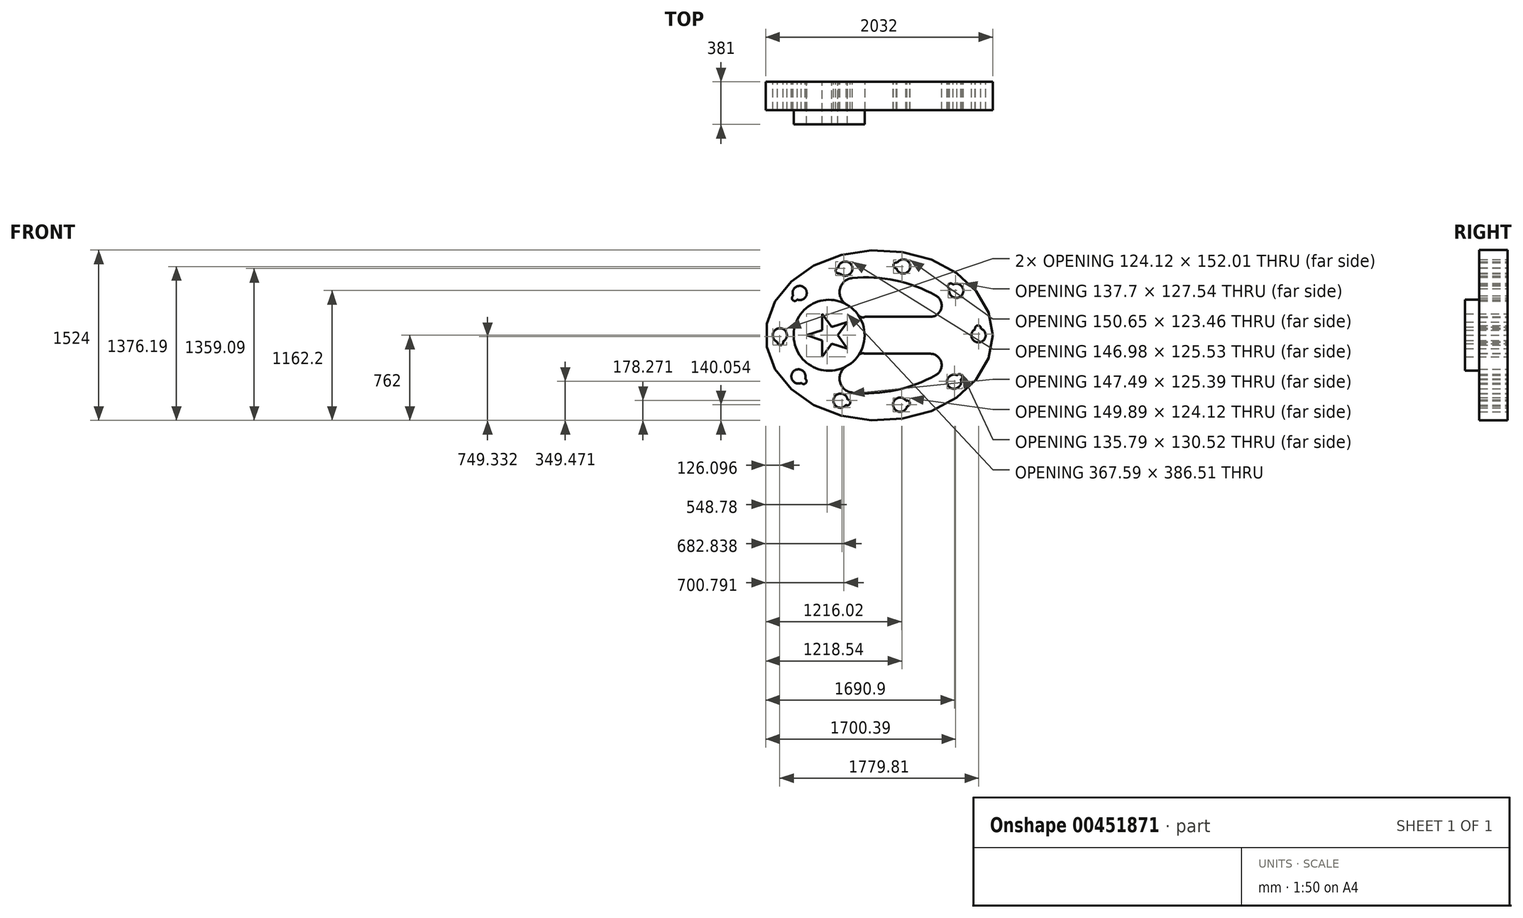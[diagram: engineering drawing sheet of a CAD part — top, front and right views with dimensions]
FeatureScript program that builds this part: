
annotation { "Feature Type Name" : "Feature", "Feature Type Description" : "" }
export const myFeature = defineFeature(function(context is Context, id is Id, definition is map)
    precondition{}
    {
        {
            var Q0;
            Q0=qCreatedBy(makeId("Front.planeOp"),FACE);
            var sketch = newSketch(context, id + "F0", { "sketchPlane" : qUnion([Q0])});
            skEllipse(sketch, "E0", {"center": v(0, 0) * mm, "majorRadius": 1016 * mm, "minorRadius": 762 * mm, "majorAxis": v(1, 0)});
            skCircle(sketch, "E1", {"center": v(-447.82, 0) * mm, "radius": 317.5 * mm});
            skArc(sketch, "E2", {"start": v(-187.82, 182.23) * mm, "mid": v(-159.63, 162.39) * mm, "end": v(-125.28, 165.1) * mm});
            skLineSegment(sketch, "E3", {"start": v(-125.28, 165.1) * mm, "end": v(457.62, 165.1) * mm});
            skArc(sketch, "E4", {"start": v(-240, 512.49) * mm, "mid": v(-351.77, 412.6) * mm, "end": v(-290.5, 275.78) * mm});
            skArc(sketch, "E5", {"start": v(457.62, 165.1) * mm, "mid": v(555.9, 240.93) * mm, "end": v(507.46, 355.23) * mm});
            skArc(sketch, "E6", {"start": v(507.46, 355.23) * mm, "mid": v(145.83, 491.38) * mm, "end": v(-240, 512.49) * mm});
            skLineSegment(sketch, "E7", {"start": v(-510.6, 193.25) * mm, "end": v(-423.83, 73.82) * mm});
            skLineSegment(sketch, "E8.1.0", {"start": v(-510.6, -193.25) * mm, "end": v(-423.83, -73.82) * mm});
            skLineSegment(sketch, "E8.1.1", {"start": v(-651.02, 0) * mm, "end": v(-510.6, 45.62) * mm});
            skLineSegment(sketch, "E8.2.0", {"start": v(-283.42, -119.44) * mm, "end": v(-370.2, 0) * mm});
            skLineSegment(sketch, "E8.2.1", {"start": v(-510.6, -193.25) * mm, "end": v(-510.6, -45.62) * mm});
            skLineSegment(sketch, "E8.3.1", {"start": v(-283.42, -119.44) * mm, "end": v(-423.83, -73.82) * mm});
            skLineSegment(sketch, "E8.4.0", {"start": v(-510.6, 193.25) * mm, "end": v(-510.6, 45.62) * mm});
            skLineSegment(sketch, "E8.4.1", {"start": v(-283.42, 119.44) * mm, "end": v(-370.2, 0) * mm});
            skFitSpline(sketch, "E9.0", {"points": [v(888.96, -7.37) * mm, v(889.02, 0) * mm, v(888.96, 7.37) * mm, v(888.72, 17.17) * mm, v(888.1, 29.4) * mm, v(886.9, 44.05) * mm, v(884.64, 63.52) * mm, v(880.63, 87.75) * mm, v(873.9, 116.67) * mm, v(865.26, 145.41) * mm, v(854.7, 173.95) * mm, v(842.22, 202.24) * mm, v(823, 239.6) * mm, v(799.9, 276.3) * mm, v(772.9, 312.12) * mm, v(750.71, 338.47) * mm, v(726.57, 364.24) * mm, v(704.83, 385.18) * mm, v(686.47, 401.56) * mm, v(672.23, 413.66) * mm, v(659.96, 423.58) * mm, v(649.9, 431.4) * mm, v(642.24, 437.23) * mm, v(634.47, 442.98) * mm, v(623.98, 450.56) * mm, v(610.63, 459.86) * mm, v(594.23, 470.72) * mm, v(571.88, 484.8) * mm, v(543.04, 501.65) * mm, v(507.09, 520.6) * mm, v(469.85, 538.25) * mm, v(418.6, 560) * mm, v(365.13, 578.95) * mm, v(309.76, 594.98) * mm, v(267.38, 605.5) * mm, v(224.23, 614.48) * mm, v(180.4, 621.9) * mm, v(135.98, 627.7) * mm, v(98.54, 631.2) * mm, v(68.38, 633.16) * mm, v(45.67, 634.22) * mm, v(26.67, 634.75) * mm, v(11.44, 634.96) * mm, v(0, 635.02) * mm, v(-11.44, 634.96) * mm, v(-26.67, 634.75) * mm, v(-45.67, 634.22) * mm, v(-68.38, 633.16) * mm, v(-98.54, 631.2) * mm, v(-135.98, 627.7) * mm, v(-180.4, 621.9) * mm, v(-224.23, 614.48) * mm, v(-267.38, 605.5) * mm, v(-309.76, 594.98) * mm, v(-365.13, 578.95) * mm, v(-418.6, 560) * mm, v(-469.85, 538.25) * mm, v(-507.09, 520.6) * mm, v(-543.04, 501.65) * mm, v(-571.88, 484.8) * mm, v(-594.23, 470.72) * mm, v(-610.63, 459.86) * mm, v(-623.98, 450.56) * mm, v(-634.47, 442.98) * mm, v(-642.24, 437.23) * mm, v(-649.9, 431.4) * mm, v(-659.96, 423.58) * mm, v(-672.23, 413.66) * mm, v(-686.47, 401.56) * mm, v(-704.83, 385.18) * mm, v(-726.57, 364.24) * mm, v(-750.71, 338.47) * mm, v(-772.9, 312.12) * mm, v(-799.9, 276.3) * mm, v(-823, 239.6) * mm, v(-842.22, 202.24) * mm, v(-854.7, 173.95) * mm, v(-865.26, 145.41) * mm, v(-873.9, 116.67) * mm, v(-880.63, 87.75) * mm, v(-884.64, 63.52) * mm, v(-886.9, 44.05) * mm, v(-888.1, 29.4) * mm, v(-888.72, 17.17) * mm, v(-888.96, 7.37) * mm, v(-889.02, 0) * mm, v(-888.96, -7.37) * mm, v(-888.72, -17.17) * mm, v(-888.1, -29.4) * mm, v(-886.9, -44.05) * mm, v(-884.64, -63.52) * mm, v(-880.63, -87.75) * mm, v(-873.9, -116.67) * mm, v(-865.26, -145.41) * mm, v(-854.7, -173.95) * mm, v(-842.22, -202.24) * mm, v(-823, -239.6) * mm, v(-799.9, -276.3) * mm, v(-772.9, -312.12) * mm, v(-750.71, -338.47) * mm, v(-726.57, -364.24) * mm, v(-704.83, -385.18) * mm, v(-686.47, -401.56) * mm, v(-672.23, -413.66) * mm, v(-659.96, -423.58) * mm, v(-649.9, -431.4) * mm, v(-642.24, -437.23) * mm, v(-634.47, -442.98) * mm, v(-623.98, -450.56) * mm, v(-610.63, -459.86) * mm, v(-594.23, -470.72) * mm, v(-571.88, -484.8) * mm, v(-543.04, -501.65) * mm, v(-507.09, -520.6) * mm, v(-469.85, -538.25) * mm, v(-418.6, -560) * mm, v(-365.13, -578.95) * mm, v(-309.76, -594.98) * mm, v(-267.38, -605.5) * mm, v(-224.23, -614.48) * mm, v(-180.4, -621.9) * mm, v(-135.98, -627.7) * mm, v(-98.54, -631.2) * mm, v(-68.38, -633.16) * mm, v(-45.67, -634.22) * mm, v(-26.67, -634.75) * mm, v(-11.44, -634.96) * mm, v(0, -635.02) * mm, v(11.44, -634.96) * mm, v(26.67, -634.75) * mm, v(45.67, -634.22) * mm, v(68.38, -633.16) * mm, v(98.54, -631.2) * mm, v(135.98, -627.7) * mm, v(180.4, -621.9) * mm, v(224.23, -614.48) * mm, v(267.38, -605.5) * mm, v(309.76, -594.98) * mm, v(365.13, -578.95) * mm, v(418.6, -560) * mm, v(469.85, -538.25) * mm, v(507.09, -520.6) * mm, v(543.04, -501.65) * mm, v(571.88, -484.8) * mm, v(594.23, -470.72) * mm, v(610.63, -459.86) * mm, v(623.98, -450.56) * mm, v(634.47, -442.98) * mm, v(642.24, -437.23) * mm, v(649.9, -431.4) * mm, v(659.96, -423.58) * mm, v(672.23, -413.66) * mm, v(686.47, -401.56) * mm, v(704.83, -385.18) * mm, v(726.57, -364.24) * mm, v(750.71, -338.47) * mm, v(772.9, -312.12) * mm, v(799.9, -276.3) * mm, v(823, -239.6) * mm, v(842.22, -202.24) * mm, v(854.7, -173.95) * mm, v(865.26, -145.41) * mm, v(873.9, -116.67) * mm, v(880.63, -87.75) * mm, v(884.64, -63.52) * mm, v(886.9, -44.05) * mm, v(888.1, -29.4) * mm, v(888.72, -17.17) * mm, v(888.96, -7.37) * mm, v(889.02, 0) * mm, v(888.96, 7.37) * mm], "construction": true});
            skArc(sketch, "E10", {"start": v(860.02, 56.5) * mm, "mid": v(893.52, -63.34) * mm, "end": v(909.66, 60.04) * mm});
            skArc(sketch, "E11", {"start": v(909.66, 60.04) * mm, "mid": v(882.67, 88.67) * mm, "end": v(860.02, 56.5) * mm});
            skArc(sketch, "E12", {"start": v(628.7, 416.03) * mm, "mid": v(739.09, 358.62) * mm, "end": v(660.02, 454.7) * mm});
            skLineSegment(sketch, "E13", {"start": v(619.82, 453.43) * mm, "end": v(619.82, 453.43) * mm});
            skLineSegment(sketch, "E14.trimOffspring", {"start": v(640.41, 438.57) * mm, "end": v(640.41, 438.57) * mm});
            skArc(sketch, "E15.trimOffspring", {"start": v(660.02, 454.7) * mm, "mid": v(620.68, 454.56) * mm, "end": v(628.7, 416.03) * mm});
            skArc(sketch, "E16", {"start": v(153.58, 600.11) * mm, "mid": v(277.86, 606.28) * mm, "end": v(161.1, 649.31) * mm});
            skLineSegment(sketch, "E17", {"start": v(177.49, 622.04) * mm, "end": v(177.49, 622.04) * mm});
            skArc(sketch, "E18.trimOffspring", {"start": v(161.1, 649.31) * mm, "mid": v(127.21, 629.32) * mm, "end": v(153.58, 600.11) * mm});
            skArc(sketch, "E19", {"start": v(-351.76, 556.3) * mm, "mid": v(-241.72, 614.39) * mm, "end": v(-365.72, 604.06) * mm});
            skArc(sketch, "E20", {"start": v(-365.72, 604.06) * mm, "mid": v(-388, 571.62) * mm, "end": v(-351.76, 556.3) * mm});
            skArc(sketch, "E21", {"start": v(-733.87, 319.18) * mm, "mid": v(-667.67, 424.54) * mm, "end": v(-769.87, 353.55) * mm});
            skArc(sketch, "E22", {"start": v(-769.87, 353.55) * mm, "mid": v(-772.92, 314.32) * mm, "end": v(-733.87, 319.18) * mm});
            skLineSegment(sketch, "E23", {"start": v(-887.37, -38.1) * mm, "end": v(-887.37, -38.1) * mm});
            skArc(sketch, "E24", {"start": v(-860.02, -56.5) * mm, "mid": v(-893.52, 63.34) * mm, "end": v(-909.66, -60.04) * mm});
            skArc(sketch, "E25.trimOffspring", {"start": v(-909.66, -60.04) * mm, "mid": v(-882.67, -88.67) * mm, "end": v(-860.02, -56.5) * mm});
            skArc(sketch, "E26", {"start": v(-662.6, -388.93) * mm, "mid": v(-769.38, -325.05) * mm, "end": v(-696.17, -425.67) * mm});
            skArc(sketch, "E27", {"start": v(-696.17, -425.67) * mm, "mid": v(-656.88, -427.86) * mm, "end": v(-662.6, -388.93) * mm});
            skLineSegment(sketch, "E28", {"start": v(-284.43, -601.19) * mm, "end": v(-284.43, -601.19) * mm});
            skArc(sketch, "E29", {"start": v(-295.9, -623.84) * mm, "mid": v(-259.93, -607.9) * mm, "end": v(-282.75, -575.84) * mm});
            skArc(sketch, "E30.trimOffspring", {"start": v(-282.75, -575.84) * mm, "mid": v(-406.9, -567.6) * mm, "end": v(-295.9, -623.84) * mm});
            skArc(sketch, "E31", {"start": v(240.48, -585.48) * mm, "mid": v(125.07, -632) * mm, "end": v(249.48, -634.43) * mm});
            skLineSegment(sketch, "E32", {"start": v(225.08, -614.03) * mm, "end": v(225.08, -614.03) * mm});
            skArc(sketch, "E33.trimOffspring", {"start": v(249.48, -634.43) * mm, "mid": v(274.96, -604.45) * mm, "end": v(240.48, -585.48) * mm});
            skLineSegment(sketch, "E34.trimOffspring", {"start": v(249.98, -609.04) * mm, "end": v(249.98, -609.04) * mm});
            skArc(sketch, "E35", {"start": v(697.3, -357.51) * mm, "mid": v(623.16, -457.45) * mm, "end": v(730.53, -394.56) * mm});
            skArc(sketch, "E36", {"start": v(730.53, -394.56) * mm, "mid": v(736.6, -355.68) * mm, "end": v(697.3, -357.51) * mm});
            skFitSpline(sketch, "E37.trimOffspring", {"points": [v(888.96, -7.37) * mm, v(889.02, 0) * mm, v(888.96, 7.37) * mm, v(888.72, 17.17) * mm, v(888.1, 29.4) * mm, v(886.9, 44.05) * mm, v(884.64, 63.52) * mm, v(880.63, 87.75) * mm, v(873.9, 116.67) * mm, v(865.26, 145.41) * mm, v(854.7, 173.95) * mm, v(842.22, 202.24) * mm, v(823, 239.6) * mm, v(799.9, 276.3) * mm, v(772.9, 312.12) * mm, v(750.71, 338.47) * mm, v(726.57, 364.24) * mm, v(704.83, 385.18) * mm, v(686.47, 401.56) * mm, v(672.23, 413.66) * mm, v(659.96, 423.58) * mm, v(649.9, 431.4) * mm, v(642.24, 437.23) * mm, v(634.47, 442.98) * mm, v(623.98, 450.56) * mm, v(610.63, 459.86) * mm, v(594.23, 470.72) * mm, v(571.88, 484.8) * mm, v(543.04, 501.65) * mm, v(507.09, 520.6) * mm, v(469.85, 538.25) * mm, v(418.6, 560) * mm, v(365.13, 578.95) * mm, v(309.76, 594.98) * mm, v(267.38, 605.5) * mm, v(224.23, 614.48) * mm, v(180.4, 621.9) * mm, v(135.98, 627.7) * mm, v(98.54, 631.2) * mm, v(68.38, 633.16) * mm, v(45.67, 634.22) * mm, v(26.67, 634.75) * mm, v(11.44, 634.96) * mm, v(0, 635.02) * mm, v(-11.44, 634.96) * mm, v(-26.67, 634.75) * mm, v(-45.67, 634.22) * mm, v(-68.38, 633.16) * mm, v(-98.54, 631.2) * mm, v(-135.98, 627.7) * mm, v(-180.4, 621.9) * mm, v(-224.23, 614.48) * mm, v(-267.38, 605.5) * mm, v(-309.76, 594.98) * mm, v(-365.13, 578.95) * mm, v(-418.6, 560) * mm, v(-469.85, 538.25) * mm, v(-507.09, 520.6) * mm, v(-543.04, 501.65) * mm, v(-571.88, 484.8) * mm, v(-594.23, 470.72) * mm, v(-610.63, 459.86) * mm, v(-623.98, 450.56) * mm, v(-634.47, 442.98) * mm, v(-642.24, 437.23) * mm, v(-649.9, 431.4) * mm, v(-659.96, 423.58) * mm, v(-672.23, 413.66) * mm, v(-686.47, 401.56) * mm, v(-704.83, 385.18) * mm, v(-726.57, 364.24) * mm, v(-750.71, 338.47) * mm, v(-772.9, 312.12) * mm, v(-799.9, 276.3) * mm, v(-823, 239.6) * mm, v(-842.22, 202.24) * mm, v(-854.7, 173.95) * mm, v(-865.26, 145.41) * mm, v(-873.9, 116.67) * mm, v(-880.63, 87.75) * mm, v(-884.64, 63.52) * mm, v(-886.9, 44.05) * mm, v(-888.1, 29.4) * mm, v(-888.72, 17.17) * mm, v(-888.96, 7.37) * mm, v(-889.02, 0) * mm, v(-888.96, -7.37) * mm, v(-888.72, -17.17) * mm, v(-888.1, -29.4) * mm, v(-886.9, -44.05) * mm, v(-884.64, -63.52) * mm, v(-880.63, -87.75) * mm, v(-873.9, -116.67) * mm, v(-865.26, -145.41) * mm, v(-854.7, -173.95) * mm, v(-842.22, -202.24) * mm, v(-823, -239.6) * mm, v(-799.9, -276.3) * mm, v(-772.9, -312.12) * mm, v(-750.71, -338.47) * mm, v(-726.57, -364.24) * mm, v(-704.83, -385.18) * mm, v(-686.47, -401.56) * mm, v(-672.23, -413.66) * mm, v(-659.96, -423.58) * mm, v(-649.9, -431.4) * mm, v(-642.24, -437.23) * mm, v(-634.47, -442.98) * mm, v(-623.98, -450.56) * mm, v(-610.63, -459.86) * mm, v(-594.23, -470.72) * mm, v(-571.88, -484.8) * mm, v(-543.04, -501.65) * mm, v(-507.09, -520.6) * mm, v(-469.85, -538.25) * mm, v(-418.6, -560) * mm, v(-365.13, -578.95) * mm, v(-309.76, -594.98) * mm, v(-267.38, -605.5) * mm, v(-224.23, -614.48) * mm, v(-180.4, -621.9) * mm, v(-135.98, -627.7) * mm, v(-98.54, -631.2) * mm, v(-68.38, -633.16) * mm, v(-45.67, -634.22) * mm, v(-26.67, -634.75) * mm, v(-11.44, -634.96) * mm, v(0, -635.02) * mm, v(11.44, -634.96) * mm, v(26.67, -634.75) * mm, v(45.67, -634.22) * mm, v(68.38, -633.16) * mm, v(98.54, -631.2) * mm, v(135.98, -627.7) * mm, v(180.4, -621.9) * mm, v(224.23, -614.48) * mm, v(267.38, -605.5) * mm, v(309.76, -594.98) * mm, v(365.13, -578.95) * mm, v(418.6, -560) * mm, v(469.85, -538.25) * mm, v(507.09, -520.6) * mm, v(543.04, -501.65) * mm, v(571.88, -484.8) * mm, v(594.23, -470.72) * mm, v(610.63, -459.86) * mm, v(623.98, -450.56) * mm, v(634.47, -442.98) * mm, v(642.24, -437.23) * mm, v(649.9, -431.4) * mm, v(659.96, -423.58) * mm, v(672.23, -413.66) * mm, v(686.47, -401.56) * mm, v(704.83, -385.18) * mm, v(726.57, -364.24) * mm, v(750.71, -338.47) * mm, v(772.9, -312.12) * mm, v(799.9, -276.3) * mm, v(823, -239.6) * mm, v(842.22, -202.24) * mm, v(854.7, -173.95) * mm, v(865.26, -145.41) * mm, v(873.9, -116.67) * mm, v(880.63, -87.75) * mm, v(884.64, -63.52) * mm, v(886.9, -44.05) * mm, v(888.1, -29.4) * mm, v(888.72, -17.17) * mm, v(888.96, -7.37) * mm, v(889.02, 0) * mm, v(888.96, 7.37) * mm], "construction": true});
            skFitSpline(sketch, "E38.trimOffspring", {"points": [v(888.96, -7.37) * mm, v(889.02, 0) * mm, v(888.96, 7.37) * mm, v(888.72, 17.17) * mm, v(888.1, 29.4) * mm, v(886.9, 44.05) * mm, v(884.64, 63.52) * mm, v(880.63, 87.75) * mm, v(873.9, 116.67) * mm, v(865.26, 145.41) * mm, v(854.7, 173.95) * mm, v(842.22, 202.24) * mm, v(823, 239.6) * mm, v(799.9, 276.3) * mm, v(772.9, 312.12) * mm, v(750.71, 338.47) * mm, v(726.57, 364.24) * mm, v(704.83, 385.18) * mm, v(686.47, 401.56) * mm, v(672.23, 413.66) * mm, v(659.96, 423.58) * mm, v(649.9, 431.4) * mm, v(642.24, 437.23) * mm, v(634.47, 442.98) * mm, v(623.98, 450.56) * mm, v(610.63, 459.86) * mm, v(594.23, 470.72) * mm, v(571.88, 484.8) * mm, v(543.04, 501.65) * mm, v(507.09, 520.6) * mm, v(469.85, 538.25) * mm, v(418.6, 560) * mm, v(365.13, 578.95) * mm, v(309.76, 594.98) * mm, v(267.38, 605.5) * mm, v(224.23, 614.48) * mm, v(180.4, 621.9) * mm, v(135.98, 627.7) * mm, v(98.54, 631.2) * mm, v(68.38, 633.16) * mm, v(45.67, 634.22) * mm, v(26.67, 634.75) * mm, v(11.44, 634.96) * mm, v(0, 635.02) * mm, v(-11.44, 634.96) * mm, v(-26.67, 634.75) * mm, v(-45.67, 634.22) * mm, v(-68.38, 633.16) * mm, v(-98.54, 631.2) * mm, v(-135.98, 627.7) * mm, v(-180.4, 621.9) * mm, v(-224.23, 614.48) * mm, v(-267.38, 605.5) * mm, v(-309.76, 594.98) * mm, v(-365.13, 578.95) * mm, v(-418.6, 560) * mm, v(-469.85, 538.25) * mm, v(-507.09, 520.6) * mm, v(-543.04, 501.65) * mm, v(-571.88, 484.8) * mm, v(-594.23, 470.72) * mm, v(-610.63, 459.86) * mm, v(-623.98, 450.56) * mm, v(-634.47, 442.98) * mm, v(-642.24, 437.23) * mm, v(-649.9, 431.4) * mm, v(-659.96, 423.58) * mm, v(-672.23, 413.66) * mm, v(-686.47, 401.56) * mm, v(-704.83, 385.18) * mm, v(-726.57, 364.24) * mm, v(-750.71, 338.47) * mm, v(-772.9, 312.12) * mm, v(-799.9, 276.3) * mm, v(-823, 239.6) * mm, v(-842.22, 202.24) * mm, v(-854.7, 173.95) * mm, v(-865.26, 145.41) * mm, v(-873.9, 116.67) * mm, v(-880.63, 87.75) * mm, v(-884.64, 63.52) * mm, v(-886.9, 44.05) * mm, v(-888.1, 29.4) * mm, v(-888.72, 17.17) * mm, v(-888.96, 7.37) * mm, v(-889.02, 0) * mm, v(-888.96, -7.37) * mm, v(-888.72, -17.17) * mm, v(-888.1, -29.4) * mm, v(-886.9, -44.05) * mm, v(-884.64, -63.52) * mm, v(-880.63, -87.75) * mm, v(-873.9, -116.67) * mm, v(-865.26, -145.41) * mm, v(-854.7, -173.95) * mm, v(-842.22, -202.24) * mm, v(-823, -239.6) * mm, v(-799.9, -276.3) * mm, v(-772.9, -312.12) * mm, v(-750.71, -338.47) * mm, v(-726.57, -364.24) * mm, v(-704.83, -385.18) * mm, v(-686.47, -401.56) * mm, v(-672.23, -413.66) * mm, v(-659.96, -423.58) * mm, v(-649.9, -431.4) * mm, v(-642.24, -437.23) * mm, v(-634.47, -442.98) * mm, v(-623.98, -450.56) * mm, v(-610.63, -459.86) * mm, v(-594.23, -470.72) * mm, v(-571.88, -484.8) * mm, v(-543.04, -501.65) * mm, v(-507.09, -520.6) * mm, v(-469.85, -538.25) * mm, v(-418.6, -560) * mm, v(-365.13, -578.95) * mm, v(-309.76, -594.98) * mm, v(-267.38, -605.5) * mm, v(-224.23, -614.48) * mm, v(-180.4, -621.9) * mm, v(-135.98, -627.7) * mm, v(-98.54, -631.2) * mm, v(-68.38, -633.16) * mm, v(-45.67, -634.22) * mm, v(-26.67, -634.75) * mm, v(-11.44, -634.96) * mm, v(0, -635.02) * mm, v(11.44, -634.96) * mm, v(26.67, -634.75) * mm, v(45.67, -634.22) * mm, v(68.38, -633.16) * mm, v(98.54, -631.2) * mm, v(135.98, -627.7) * mm, v(180.4, -621.9) * mm, v(224.23, -614.48) * mm, v(267.38, -605.5) * mm, v(309.76, -594.98) * mm, v(365.13, -578.95) * mm, v(418.6, -560) * mm, v(469.85, -538.25) * mm, v(507.09, -520.6) * mm, v(543.04, -501.65) * mm, v(571.88, -484.8) * mm, v(594.23, -470.72) * mm, v(610.63, -459.86) * mm, v(623.98, -450.56) * mm, v(634.47, -442.98) * mm, v(642.24, -437.23) * mm, v(649.9, -431.4) * mm, v(659.96, -423.58) * mm, v(672.23, -413.66) * mm, v(686.47, -401.56) * mm, v(704.83, -385.18) * mm, v(726.57, -364.24) * mm, v(750.71, -338.47) * mm, v(772.9, -312.12) * mm, v(799.9, -276.3) * mm, v(823, -239.6) * mm, v(842.22, -202.24) * mm, v(854.7, -173.95) * mm, v(865.26, -145.41) * mm, v(873.9, -116.67) * mm, v(880.63, -87.75) * mm, v(884.64, -63.52) * mm, v(886.9, -44.05) * mm, v(888.1, -29.4) * mm, v(888.72, -17.17) * mm, v(888.96, -7.37) * mm, v(889.02, 0) * mm, v(888.96, 7.37) * mm], "construction": true});
            skFitSpline(sketch, "E39.trimOffspring", {"points": [v(888.96, -7.37) * mm, v(889.02, 0) * mm, v(888.96, 7.37) * mm, v(888.72, 17.17) * mm, v(888.1, 29.4) * mm, v(886.9, 44.05) * mm, v(884.64, 63.52) * mm, v(880.63, 87.75) * mm, v(873.9, 116.67) * mm, v(865.26, 145.41) * mm, v(854.7, 173.95) * mm, v(842.22, 202.24) * mm, v(823, 239.6) * mm, v(799.9, 276.3) * mm, v(772.9, 312.12) * mm, v(750.71, 338.47) * mm, v(726.57, 364.24) * mm, v(704.83, 385.18) * mm, v(686.47, 401.56) * mm, v(672.23, 413.66) * mm, v(659.96, 423.58) * mm, v(649.9, 431.4) * mm, v(642.24, 437.23) * mm, v(634.47, 442.98) * mm, v(623.98, 450.56) * mm, v(610.63, 459.86) * mm, v(594.23, 470.72) * mm, v(571.88, 484.8) * mm, v(543.04, 501.65) * mm, v(507.09, 520.6) * mm, v(469.85, 538.25) * mm, v(418.6, 560) * mm, v(365.13, 578.95) * mm, v(309.76, 594.98) * mm, v(267.38, 605.5) * mm, v(224.23, 614.48) * mm, v(180.4, 621.9) * mm, v(135.98, 627.7) * mm, v(98.54, 631.2) * mm, v(68.38, 633.16) * mm, v(45.67, 634.22) * mm, v(26.67, 634.75) * mm, v(11.44, 634.96) * mm, v(0, 635.02) * mm, v(-11.44, 634.96) * mm, v(-26.67, 634.75) * mm, v(-45.67, 634.22) * mm, v(-68.38, 633.16) * mm, v(-98.54, 631.2) * mm, v(-135.98, 627.7) * mm, v(-180.4, 621.9) * mm, v(-224.23, 614.48) * mm, v(-267.38, 605.5) * mm, v(-309.76, 594.98) * mm, v(-365.13, 578.95) * mm, v(-418.6, 560) * mm, v(-469.85, 538.25) * mm, v(-507.09, 520.6) * mm, v(-543.04, 501.65) * mm, v(-571.88, 484.8) * mm, v(-594.23, 470.72) * mm, v(-610.63, 459.86) * mm, v(-623.98, 450.56) * mm, v(-634.47, 442.98) * mm, v(-642.24, 437.23) * mm, v(-649.9, 431.4) * mm, v(-659.96, 423.58) * mm, v(-672.23, 413.66) * mm, v(-686.47, 401.56) * mm, v(-704.83, 385.18) * mm, v(-726.57, 364.24) * mm, v(-750.71, 338.47) * mm, v(-772.9, 312.12) * mm, v(-799.9, 276.3) * mm, v(-823, 239.6) * mm, v(-842.22, 202.24) * mm, v(-854.7, 173.95) * mm, v(-865.26, 145.41) * mm, v(-873.9, 116.67) * mm, v(-880.63, 87.75) * mm, v(-884.64, 63.52) * mm, v(-886.9, 44.05) * mm, v(-888.1, 29.4) * mm, v(-888.72, 17.17) * mm, v(-888.96, 7.37) * mm, v(-889.02, 0) * mm, v(-888.96, -7.37) * mm, v(-888.72, -17.17) * mm, v(-888.1, -29.4) * mm, v(-886.9, -44.05) * mm, v(-884.64, -63.52) * mm, v(-880.63, -87.75) * mm, v(-873.9, -116.67) * mm, v(-865.26, -145.41) * mm, v(-854.7, -173.95) * mm, v(-842.22, -202.24) * mm, v(-823, -239.6) * mm, v(-799.9, -276.3) * mm, v(-772.9, -312.12) * mm, v(-750.71, -338.47) * mm, v(-726.57, -364.24) * mm, v(-704.83, -385.18) * mm, v(-686.47, -401.56) * mm, v(-672.23, -413.66) * mm, v(-659.96, -423.58) * mm, v(-649.9, -431.4) * mm, v(-642.24, -437.23) * mm, v(-634.47, -442.98) * mm, v(-623.98, -450.56) * mm, v(-610.63, -459.86) * mm, v(-594.23, -470.72) * mm, v(-571.88, -484.8) * mm, v(-543.04, -501.65) * mm, v(-507.09, -520.6) * mm, v(-469.85, -538.25) * mm, v(-418.6, -560) * mm, v(-365.13, -578.95) * mm, v(-309.76, -594.98) * mm, v(-267.38, -605.5) * mm, v(-224.23, -614.48) * mm, v(-180.4, -621.9) * mm, v(-135.98, -627.7) * mm, v(-98.54, -631.2) * mm, v(-68.38, -633.16) * mm, v(-45.67, -634.22) * mm, v(-26.67, -634.75) * mm, v(-11.44, -634.96) * mm, v(0, -635.02) * mm, v(11.44, -634.96) * mm, v(26.67, -634.75) * mm, v(45.67, -634.22) * mm, v(68.38, -633.16) * mm, v(98.54, -631.2) * mm, v(135.98, -627.7) * mm, v(180.4, -621.9) * mm, v(224.23, -614.48) * mm, v(267.38, -605.5) * mm, v(309.76, -594.98) * mm, v(365.13, -578.95) * mm, v(418.6, -560) * mm, v(469.85, -538.25) * mm, v(507.09, -520.6) * mm, v(543.04, -501.65) * mm, v(571.88, -484.8) * mm, v(594.23, -470.72) * mm, v(610.63, -459.86) * mm, v(623.98, -450.56) * mm, v(634.47, -442.98) * mm, v(642.24, -437.23) * mm, v(649.9, -431.4) * mm, v(659.96, -423.58) * mm, v(672.23, -413.66) * mm, v(686.47, -401.56) * mm, v(704.83, -385.18) * mm, v(726.57, -364.24) * mm, v(750.71, -338.47) * mm, v(772.9, -312.12) * mm, v(799.9, -276.3) * mm, v(823, -239.6) * mm, v(842.22, -202.24) * mm, v(854.7, -173.95) * mm, v(865.26, -145.41) * mm, v(873.9, -116.67) * mm, v(880.63, -87.75) * mm, v(884.64, -63.52) * mm, v(886.9, -44.05) * mm, v(888.1, -29.4) * mm, v(888.72, -17.17) * mm, v(888.96, -7.37) * mm, v(889.02, 0) * mm, v(888.96, 7.37) * mm], "construction": true});
            skFitSpline(sketch, "E40.trimOffspring", {"points": [v(888.96, -7.37) * mm, v(889.02, 0) * mm, v(888.96, 7.37) * mm, v(888.72, 17.17) * mm, v(888.1, 29.4) * mm, v(886.9, 44.05) * mm, v(884.64, 63.52) * mm, v(880.63, 87.75) * mm, v(873.9, 116.67) * mm, v(865.26, 145.41) * mm, v(854.7, 173.95) * mm, v(842.22, 202.24) * mm, v(823, 239.6) * mm, v(799.9, 276.3) * mm, v(772.9, 312.12) * mm, v(750.71, 338.47) * mm, v(726.57, 364.24) * mm, v(704.83, 385.18) * mm, v(686.47, 401.56) * mm, v(672.23, 413.66) * mm, v(659.96, 423.58) * mm, v(649.9, 431.4) * mm, v(642.24, 437.23) * mm, v(634.47, 442.98) * mm, v(623.98, 450.56) * mm, v(610.63, 459.86) * mm, v(594.23, 470.72) * mm, v(571.88, 484.8) * mm, v(543.04, 501.65) * mm, v(507.09, 520.6) * mm, v(469.85, 538.25) * mm, v(418.6, 560) * mm, v(365.13, 578.95) * mm, v(309.76, 594.98) * mm, v(267.38, 605.5) * mm, v(224.23, 614.48) * mm, v(180.4, 621.9) * mm, v(135.98, 627.7) * mm, v(98.54, 631.2) * mm, v(68.38, 633.16) * mm, v(45.67, 634.22) * mm, v(26.67, 634.75) * mm, v(11.44, 634.96) * mm, v(0, 635.02) * mm, v(-11.44, 634.96) * mm, v(-26.67, 634.75) * mm, v(-45.67, 634.22) * mm, v(-68.38, 633.16) * mm, v(-98.54, 631.2) * mm, v(-135.98, 627.7) * mm, v(-180.4, 621.9) * mm, v(-224.23, 614.48) * mm, v(-267.38, 605.5) * mm, v(-309.76, 594.98) * mm, v(-365.13, 578.95) * mm, v(-418.6, 560) * mm, v(-469.85, 538.25) * mm, v(-507.09, 520.6) * mm, v(-543.04, 501.65) * mm, v(-571.88, 484.8) * mm, v(-594.23, 470.72) * mm, v(-610.63, 459.86) * mm, v(-623.98, 450.56) * mm, v(-634.47, 442.98) * mm, v(-642.24, 437.23) * mm, v(-649.9, 431.4) * mm, v(-659.96, 423.58) * mm, v(-672.23, 413.66) * mm, v(-686.47, 401.56) * mm, v(-704.83, 385.18) * mm, v(-726.57, 364.24) * mm, v(-750.71, 338.47) * mm, v(-772.9, 312.12) * mm, v(-799.9, 276.3) * mm, v(-823, 239.6) * mm, v(-842.22, 202.24) * mm, v(-854.7, 173.95) * mm, v(-865.26, 145.41) * mm, v(-873.9, 116.67) * mm, v(-880.63, 87.75) * mm, v(-884.64, 63.52) * mm, v(-886.9, 44.05) * mm, v(-888.1, 29.4) * mm, v(-888.72, 17.17) * mm, v(-888.96, 7.37) * mm, v(-889.02, 0) * mm, v(-888.96, -7.37) * mm, v(-888.72, -17.17) * mm, v(-888.1, -29.4) * mm, v(-886.9, -44.05) * mm, v(-884.64, -63.52) * mm, v(-880.63, -87.75) * mm, v(-873.9, -116.67) * mm, v(-865.26, -145.41) * mm, v(-854.7, -173.95) * mm, v(-842.22, -202.24) * mm, v(-823, -239.6) * mm, v(-799.9, -276.3) * mm, v(-772.9, -312.12) * mm, v(-750.71, -338.47) * mm, v(-726.57, -364.24) * mm, v(-704.83, -385.18) * mm, v(-686.47, -401.56) * mm, v(-672.23, -413.66) * mm, v(-659.96, -423.58) * mm, v(-649.9, -431.4) * mm, v(-642.24, -437.23) * mm, v(-634.47, -442.98) * mm, v(-623.98, -450.56) * mm, v(-610.63, -459.86) * mm, v(-594.23, -470.72) * mm, v(-571.88, -484.8) * mm, v(-543.04, -501.65) * mm, v(-507.09, -520.6) * mm, v(-469.85, -538.25) * mm, v(-418.6, -560) * mm, v(-365.13, -578.95) * mm, v(-309.76, -594.98) * mm, v(-267.38, -605.5) * mm, v(-224.23, -614.48) * mm, v(-180.4, -621.9) * mm, v(-135.98, -627.7) * mm, v(-98.54, -631.2) * mm, v(-68.38, -633.16) * mm, v(-45.67, -634.22) * mm, v(-26.67, -634.75) * mm, v(-11.44, -634.96) * mm, v(0, -635.02) * mm, v(11.44, -634.96) * mm, v(26.67, -634.75) * mm, v(45.67, -634.22) * mm, v(68.38, -633.16) * mm, v(98.54, -631.2) * mm, v(135.98, -627.7) * mm, v(180.4, -621.9) * mm, v(224.23, -614.48) * mm, v(267.38, -605.5) * mm, v(309.76, -594.98) * mm, v(365.13, -578.95) * mm, v(418.6, -560) * mm, v(469.85, -538.25) * mm, v(507.09, -520.6) * mm, v(543.04, -501.65) * mm, v(571.88, -484.8) * mm, v(594.23, -470.72) * mm, v(610.63, -459.86) * mm, v(623.98, -450.56) * mm, v(634.47, -442.98) * mm, v(642.24, -437.23) * mm, v(649.9, -431.4) * mm, v(659.96, -423.58) * mm, v(672.23, -413.66) * mm, v(686.47, -401.56) * mm, v(704.83, -385.18) * mm, v(726.57, -364.24) * mm, v(750.71, -338.47) * mm, v(772.9, -312.12) * mm, v(799.9, -276.3) * mm, v(823, -239.6) * mm, v(842.22, -202.24) * mm, v(854.7, -173.95) * mm, v(865.26, -145.41) * mm, v(873.9, -116.67) * mm, v(880.63, -87.75) * mm, v(884.64, -63.52) * mm, v(886.9, -44.05) * mm, v(888.1, -29.4) * mm, v(888.72, -17.17) * mm, v(888.96, -7.37) * mm, v(889.02, 0) * mm, v(888.96, 7.37) * mm], "construction": true});
            skFitSpline(sketch, "E41.trimOffspring", {"points": [v(888.96, -7.37) * mm, v(889.02, 0) * mm, v(888.96, 7.37) * mm, v(888.72, 17.17) * mm, v(888.1, 29.4) * mm, v(886.9, 44.05) * mm, v(884.64, 63.52) * mm, v(880.63, 87.75) * mm, v(873.9, 116.67) * mm, v(865.26, 145.41) * mm, v(854.7, 173.95) * mm, v(842.22, 202.24) * mm, v(823, 239.6) * mm, v(799.9, 276.3) * mm, v(772.9, 312.12) * mm, v(750.71, 338.47) * mm, v(726.57, 364.24) * mm, v(704.83, 385.18) * mm, v(686.47, 401.56) * mm, v(672.23, 413.66) * mm, v(659.96, 423.58) * mm, v(649.9, 431.4) * mm, v(642.24, 437.23) * mm, v(634.47, 442.98) * mm, v(623.98, 450.56) * mm, v(610.63, 459.86) * mm, v(594.23, 470.72) * mm, v(571.88, 484.8) * mm, v(543.04, 501.65) * mm, v(507.09, 520.6) * mm, v(469.85, 538.25) * mm, v(418.6, 560) * mm, v(365.13, 578.95) * mm, v(309.76, 594.98) * mm, v(267.38, 605.5) * mm, v(224.23, 614.48) * mm, v(180.4, 621.9) * mm, v(135.98, 627.7) * mm, v(98.54, 631.2) * mm, v(68.38, 633.16) * mm, v(45.67, 634.22) * mm, v(26.67, 634.75) * mm, v(11.44, 634.96) * mm, v(0, 635.02) * mm, v(-11.44, 634.96) * mm, v(-26.67, 634.75) * mm, v(-45.67, 634.22) * mm, v(-68.38, 633.16) * mm, v(-98.54, 631.2) * mm, v(-135.98, 627.7) * mm, v(-180.4, 621.9) * mm, v(-224.23, 614.48) * mm, v(-267.38, 605.5) * mm, v(-309.76, 594.98) * mm, v(-365.13, 578.95) * mm, v(-418.6, 560) * mm, v(-469.85, 538.25) * mm, v(-507.09, 520.6) * mm, v(-543.04, 501.65) * mm, v(-571.88, 484.8) * mm, v(-594.23, 470.72) * mm, v(-610.63, 459.86) * mm, v(-623.98, 450.56) * mm, v(-634.47, 442.98) * mm, v(-642.24, 437.23) * mm, v(-649.9, 431.4) * mm, v(-659.96, 423.58) * mm, v(-672.23, 413.66) * mm, v(-686.47, 401.56) * mm, v(-704.83, 385.18) * mm, v(-726.57, 364.24) * mm, v(-750.71, 338.47) * mm, v(-772.9, 312.12) * mm, v(-799.9, 276.3) * mm, v(-823, 239.6) * mm, v(-842.22, 202.24) * mm, v(-854.7, 173.95) * mm, v(-865.26, 145.41) * mm, v(-873.9, 116.67) * mm, v(-880.63, 87.75) * mm, v(-884.64, 63.52) * mm, v(-886.9, 44.05) * mm, v(-888.1, 29.4) * mm, v(-888.72, 17.17) * mm, v(-888.96, 7.37) * mm, v(-889.02, 0) * mm, v(-888.96, -7.37) * mm, v(-888.72, -17.17) * mm, v(-888.1, -29.4) * mm, v(-886.9, -44.05) * mm, v(-884.64, -63.52) * mm, v(-880.63, -87.75) * mm, v(-873.9, -116.67) * mm, v(-865.26, -145.41) * mm, v(-854.7, -173.95) * mm, v(-842.22, -202.24) * mm, v(-823, -239.6) * mm, v(-799.9, -276.3) * mm, v(-772.9, -312.12) * mm, v(-750.71, -338.47) * mm, v(-726.57, -364.24) * mm, v(-704.83, -385.18) * mm, v(-686.47, -401.56) * mm, v(-672.23, -413.66) * mm, v(-659.96, -423.58) * mm, v(-649.9, -431.4) * mm, v(-642.24, -437.23) * mm, v(-634.47, -442.98) * mm, v(-623.98, -450.56) * mm, v(-610.63, -459.86) * mm, v(-594.23, -470.72) * mm, v(-571.88, -484.8) * mm, v(-543.04, -501.65) * mm, v(-507.09, -520.6) * mm, v(-469.85, -538.25) * mm, v(-418.6, -560) * mm, v(-365.13, -578.95) * mm, v(-309.76, -594.98) * mm, v(-267.38, -605.5) * mm, v(-224.23, -614.48) * mm, v(-180.4, -621.9) * mm, v(-135.98, -627.7) * mm, v(-98.54, -631.2) * mm, v(-68.38, -633.16) * mm, v(-45.67, -634.22) * mm, v(-26.67, -634.75) * mm, v(-11.44, -634.96) * mm, v(0, -635.02) * mm, v(11.44, -634.96) * mm, v(26.67, -634.75) * mm, v(45.67, -634.22) * mm, v(68.38, -633.16) * mm, v(98.54, -631.2) * mm, v(135.98, -627.7) * mm, v(180.4, -621.9) * mm, v(224.23, -614.48) * mm, v(267.38, -605.5) * mm, v(309.76, -594.98) * mm, v(365.13, -578.95) * mm, v(418.6, -560) * mm, v(469.85, -538.25) * mm, v(507.09, -520.6) * mm, v(543.04, -501.65) * mm, v(571.88, -484.8) * mm, v(594.23, -470.72) * mm, v(610.63, -459.86) * mm, v(623.98, -450.56) * mm, v(634.47, -442.98) * mm, v(642.24, -437.23) * mm, v(649.9, -431.4) * mm, v(659.96, -423.58) * mm, v(672.23, -413.66) * mm, v(686.47, -401.56) * mm, v(704.83, -385.18) * mm, v(726.57, -364.24) * mm, v(750.71, -338.47) * mm, v(772.9, -312.12) * mm, v(799.9, -276.3) * mm, v(823, -239.6) * mm, v(842.22, -202.24) * mm, v(854.7, -173.95) * mm, v(865.26, -145.41) * mm, v(873.9, -116.67) * mm, v(880.63, -87.75) * mm, v(884.64, -63.52) * mm, v(886.9, -44.05) * mm, v(888.1, -29.4) * mm, v(888.72, -17.17) * mm, v(888.96, -7.37) * mm, v(889.02, 0) * mm, v(888.96, 7.37) * mm], "construction": true});
            skLineSegment(sketch, "E42.MirrorCS", {"start": v(-125.28, -165.1) * mm, "end": v(457.62, -165.1) * mm});
            skArc(sketch, "E43.MirrorCS", {"start": v(457.62, -165.1) * mm, "mid": v(555.9, -240.93) * mm, "end": v(507.46, -355.23) * mm});
            skArc(sketch, "E44.MirrorCS", {"start": v(507.46, -355.23) * mm, "mid": v(145.83, -491.38) * mm, "end": v(-240, -512.49) * mm});
            skArc(sketch, "E45.MirrorCS", {"start": v(-240, -512.49) * mm, "mid": v(-351.77, -412.6) * mm, "end": v(-290.5, -275.78) * mm});
            skArc(sketch, "E46.MirrorCS", {"start": v(-187.82, -182.23) * mm, "mid": v(-159.63, -162.39) * mm, "end": v(-125.28, -165.1) * mm});
            skPoint(sketch, "E47.start.orphan", {"position": v(-130.32, 0) * mm});
            skLineSegment(sketch, "E48", {"start": v(-510.6, 45.62) * mm, "end": v(-510.6, 193.25) * mm});
            skLineSegment(sketch, "E49", {"start": v(-510.6, -45.62) * mm, "end": v(-651.02, 0) * mm});
            skLineSegment(sketch, "E50", {"start": v(-423.83, 73.82) * mm, "end": v(-283.42, 119.44) * mm});
            skSolve(sketch);
        }
        {
            var Q0;
            Q0=makeQuery(id+"F0.imprint","IMPRINT",FACE,{"disambiguationData":[TD([[makeQuery(id+"F0.imprint","IMPRINT",EDGE,{"derivedFrom":sQuery(id+"F0.wireOp",EDGE,"E0")}),1.0]])]});
            extrude(context, id + "F1", {"entities" : qUnion([Q0]), "depth" : 254 * mm});
        }
        {
            var Q0;
            Q0=makeQuery(id+"F0.imprint","IMPRINT",FACE,{"disambiguationData":[TD([[makeQuery(id+"F0.imprint","IMPRINT",EDGE,{"derivedFrom":sQuery(id+"F0.wireOp",EDGE,"E7")}),1.0]])]});
            extrude(context, id + "F2", {"entities" : qUnion([Q0]), "operationType" : NewBodyOperationType.ADD, "depth" : 381 * mm});
        }
    });
